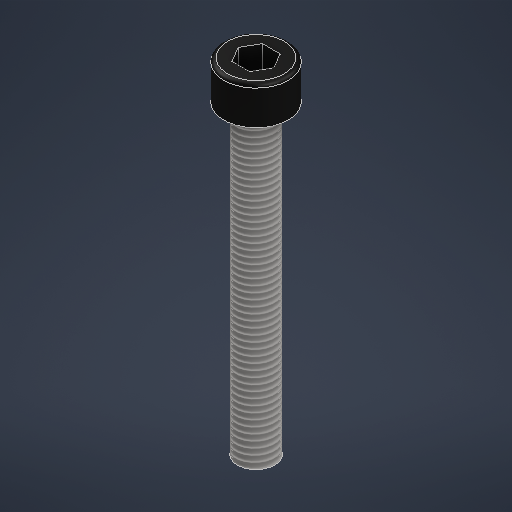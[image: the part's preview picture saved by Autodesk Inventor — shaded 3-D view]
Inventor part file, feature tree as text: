
AUTODESK INVENTOR PART (.ipt)
format: ipt  version: 2025.1 (Build 291241000, 241)  size: 262,144 bytes
history: native  units: mm
features: extrude x3, sketch x1, fillet x1, thread x1
ambient origin geometry x8: Origin, YZ Plane, XZ Plane, XY Plane, X Axis, Y Axis, Z Axis, Center Point
bodies: Solid1 (feature_tree)
feature tree (6):
  sketch  "Sketch1"  dims[d0=4.88mm d1=8.4mm d2=5.0mm d3=0.0mm d4=40.0mm d5=0.0mm d8=4.0mm d9=3.0mm d10=0.0mm d11=0.5mm d12=20.0mm d13=0.0mm]
  extrude  "Extrusion1"  Depth=0.5mm
  extrude  "Extrusion2"  Depth=5.0mm TaperAngle=0.0deg
  extrude  "Extrusion3"  Depth=40.0mm
  fillet  "Fillet1"  [1 undecoded]
  thread  "Thread2"  [1 undecoded]
note: 2 required parameter values undecoded (feature->parameter linkage not recoverable at this tier; creation-order binding heuristic only, values carry confidence <= 0.55)
